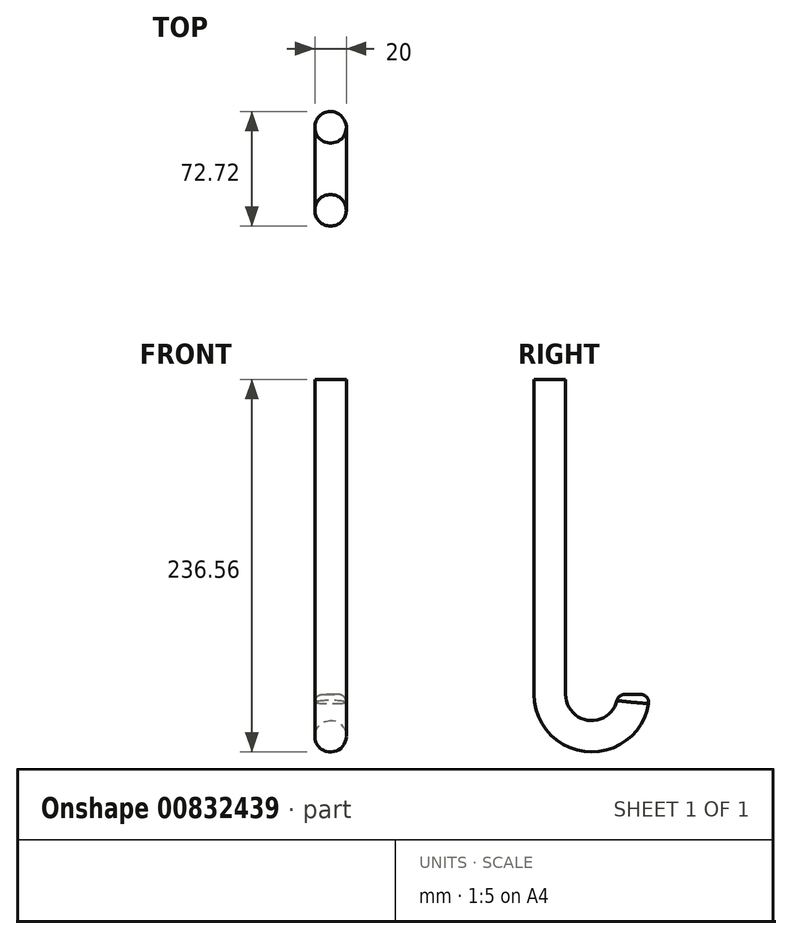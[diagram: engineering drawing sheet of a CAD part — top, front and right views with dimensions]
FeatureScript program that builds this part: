
annotation { "Feature Type Name" : "Feature", "Feature Type Description" : "" }
export const myFeature = defineFeature(function(context is Context, id is Id, definition is map)
    precondition{}
    {
        {
            var Q0;
            Q0=qCreatedBy(makeId("Top.planeOp"),FACE);
            var sketch = newSketch(context, id + "F0", { "sketchPlane" : qUnion([Q0])});
            skCircle(sketch, "E0", {"center": v(0, 0) * mm, "radius": 10 * mm});
            skLineSegment(sketch, "E1", {"start": v(-34.43, 26.56) * mm, "end": v(34.43, 26.56) * mm});
            skSolve(sketch);
        }
        {
            var Q0;
            Q0=makeQuery(id+"F0.imprint","IMPRINT",FACE,{"disambiguationData":[TD([[makeQuery(id+"F0.imprint","IMPRINT",EDGE,{"derivedFrom":sQuery(id+"F0.wireOp",EDGE,"E0")}),1.0]])]});
            var Q1;
            Q1=sQuery(id+"F0.wireOp",EDGE,"E1");
            revolve(context, id + "F1", {"surfaceOperationType" : NewSurfaceOperationType.NEW, "entities" : qUnion([Q0]), "axis" : qUnion([Q1]), "revolveType" : RevolveType.ONE_DIRECTION, "angle" : 180 * degree});
        }
        {
            var Q0;
            Q0=makeQuery(id+"F1.opRevolve","CAP_FACE",FACE,{"disambiguationData":[OSD([sQuery(id+"F0.wireOp",EDGE,"E0")])],"isStart":false});
            fillet(context, id + "F2", {"entities" : qUnion([Q0]), "radius" : 5 * mm, "tangentPropagation" : true, "allowEdgeOverflow" : false});
        }
        {
            var Q0;
            Q0=makeQuery(id+"F0.imprint","IMPRINT",FACE,{"disambiguationData":[TD([[makeQuery(id+"F0.imprint","IMPRINT",EDGE,{"derivedFrom":sQuery(id+"F0.wireOp",EDGE,"E0")}),1.0]])]});
            extrude(context, id + "F3", {"entities" : qUnion([Q0]), "operationType" : NewBodyOperationType.ADD, "depth" : 200 * mm, "offsetDistance" : 25 * mm});
        }
        {
            var Q0;
            Q0=qCreatedBy(makeId("Top.planeOp"),FACE);
            cPlane(context, id + "F4", {"entities" : qUnion([Q0]), "cplaneType" : CPlaneType.OFFSET, "offset" : 200 * mm, "width" : 150 * mm, "height" : 150 * mm});
        }
    });
